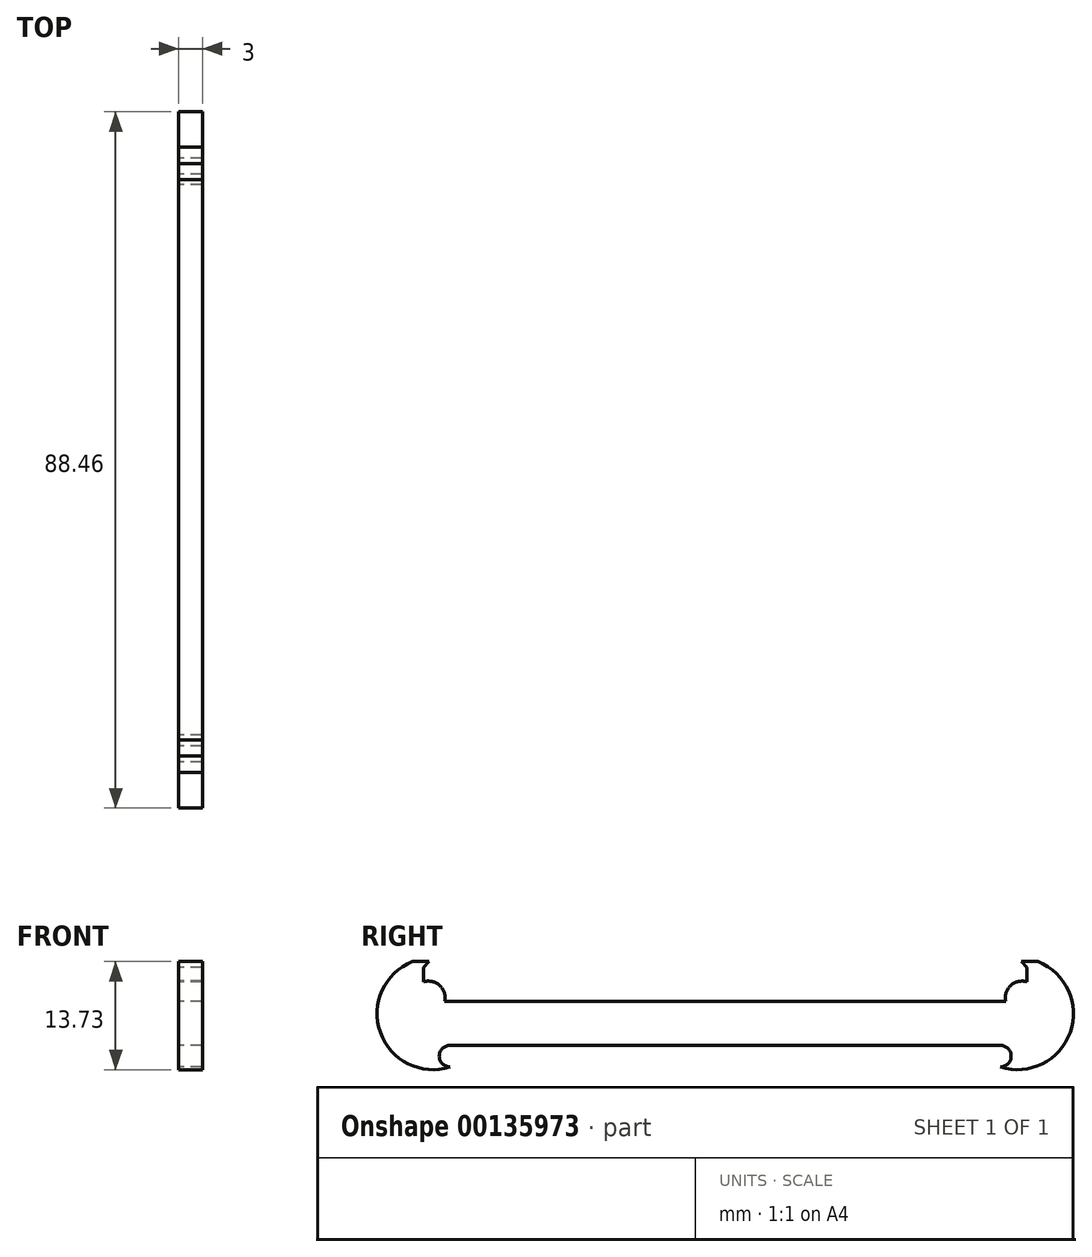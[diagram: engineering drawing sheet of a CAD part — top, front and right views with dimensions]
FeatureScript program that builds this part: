
annotation { "Feature Type Name" : "Feature", "Feature Type Description" : "" }
export const myFeature = defineFeature(function(context is Context, id is Id, definition is map)
    precondition{}
    {
        {
            var Q0;
            Q0=qCreatedBy(makeId("Right.planeOp"),FACE);
            var sketch = newSketch(context, id + "F0", { "sketchPlane" : qUnion([Q0])});
            skLineSegment(sketch, "E0", {"start": v(0, 6.62) * mm, "end": v(0, -8.38) * mm, "construction": true});
            skLineSegment(sketch, "E1", {"start": v(0, -0.88) * mm, "end": v(34.95, -0.88) * mm});
            skPoint(sketch, "E1.endSnap0", {"position": v(0, -0.88) * mm});
            skLineSegment(sketch, "E2", {"start": v(38.35, 7.2) * mm, "end": v(38.35, 9.04) * mm});
            skLineSegment(sketch, "E3", {"start": v(38.35, 9.04) * mm, "end": v(37.63, 9.77) * mm});
            skLineSegment(sketch, "E4", {"start": v(37.63, 9.77) * mm, "end": v(39.72, 9.77) * mm});
            skLineSegment(sketch, "E5", {"start": v(35.65, 4.7) * mm, "end": v(0, 4.7) * mm});
            skArc(sketch, "E6", {"start": v(34.95, -3.62) * mm, "mid": v(43.81, 0.77) * mm, "end": v(39.72, 9.77) * mm});
            skArc(sketch, "E7", {"start": v(34.95, -3.62) * mm, "mid": v(36.32, -2.25) * mm, "end": v(34.95, -0.88) * mm});
            skArc(sketch, "E8", {"start": v(38.35, 7.2) * mm, "mid": v(36.27, 6.73) * mm, "end": v(35.65, 4.7) * mm});
            skLineSegment(sketch, "E9.MirrorCS", {"start": v(-38.35, 7.2) * mm, "end": v(-38.35, 9.04) * mm});
            skLineSegment(sketch, "E10.MirrorCS", {"start": v(-38.35, 9.04) * mm, "end": v(-37.63, 9.77) * mm});
            skLineSegment(sketch, "E11.MirrorCS", {"start": v(0, -0.88) * mm, "end": v(-34.95, -0.88) * mm});
            skArc(sketch, "E12.MirrorCS", {"start": v(-38.35, 7.2) * mm, "mid": v(-36.27, 6.73) * mm, "end": v(-35.65, 4.7) * mm});
            skArc(sketch, "E13.MirrorCS", {"start": v(-34.95, -3.62) * mm, "mid": v(-36.32, -2.25) * mm, "end": v(-34.95, -0.88) * mm});
            skLineSegment(sketch, "E14.MirrorCS", {"start": v(-37.63, 9.77) * mm, "end": v(-39.72, 9.77) * mm});
            skLineSegment(sketch, "E15.MirrorCS", {"start": v(-35.65, 4.7) * mm, "end": v(0, 4.7) * mm});
            skArc(sketch, "E16.MirrorCS", {"start": v(-34.95, -3.62) * mm, "mid": v(-43.81, 0.77) * mm, "end": v(-39.72, 9.77) * mm});
            skSolve(sketch);
        }
        {
            var Q0;
            Q0=makeQuery(id+"F0.imprint","IMPRINT",FACE,{"disambiguationData":[TD([[makeQuery(id+"F0.imprint","IMPRINT",EDGE,{"derivedFrom":sQuery(id+"F0.wireOp",EDGE,"E1")}),1.0]])]});
            extrude(context, id + "F1", {"entities" : qUnion([Q0]), "depth" : 3 * mm});
        }
    });
